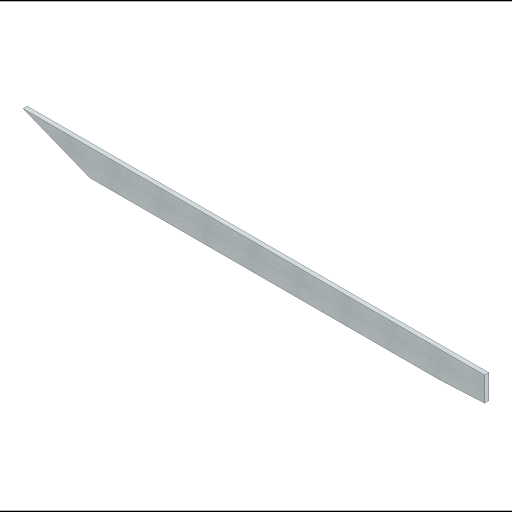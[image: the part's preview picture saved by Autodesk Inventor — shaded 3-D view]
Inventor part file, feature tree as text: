
AUTODESK INVENTOR PART (.ipt)
format: ipt  version: 2023 (Build 270158000, 158)  size: 120,832 bytes
history: native  units: in
note: dims shown in document units (in); Inventor stores cm internally (conversion verified against a paired STEP export)
features: extrude x1, sketch x1
ambient origin geometry x8: Origin, YZ Plane, XZ Plane, XY Plane, X Axis, Y Axis, Z Axis, Center Point
bodies: Solid1 (feature_tree)
feature tree (2):
  extrude  "Extrusion1"  Depth=52.0in
  sketch  "Sketch1"  dims[d0=3.0in d1=52.0in d2=0.0206in d3=5.0in d5=0.1494in d6=0.47in d7=0.0in]
